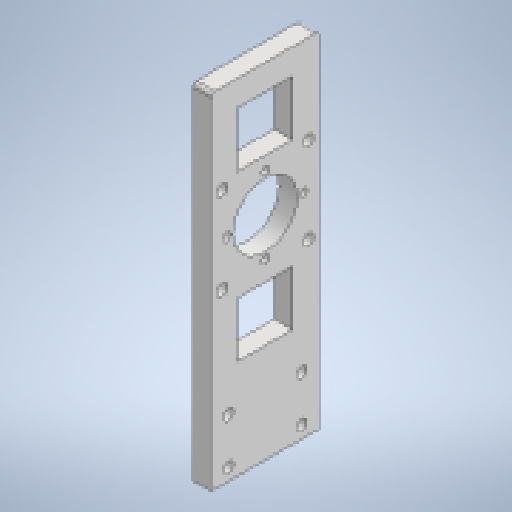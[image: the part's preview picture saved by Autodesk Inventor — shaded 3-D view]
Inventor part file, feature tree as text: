
AUTODESK INVENTOR PART (.ipt)
format: ipt  version: 2023 (Build 270158000, 158)  size: 200,192 bytes
history: native  units: mm
features: extrude x3, sketch x3
ambient origin geometry x8: Origin, YZ Plane, XZ Plane, XY Plane, X Axis, Y Axis, Z Axis, Center Point
bodies: Solid1 (feature_tree)
feature tree (6):
  extrude  "Extrusion1"  Depth=25.0mm
  extrude  "Extrusion2"  Depth=58.8mm
  extrude  "Extrusion3"  Depth=10.0mm TaperAngle=0.0deg
  sketch  "Sketch1"  dims[d0=6.0mm d1=25.0mm]
  sketch  "Sketch3"  dims[d2=40.0mm d3=58.8mm]
  sketch  "Sketch4"  dims[d4=38.2mm d5=10.0mm d6=0.0mm d7=150.0mm d8=2.0mm d9=30.0mm d12=60.0mm d13=16.0mm d14=10.0mm d15=0.0mm d16=47.14mm d17=6.0mm d18=56.4mm d19=35.0mm d20=20.0mm d21=0.0mm d22=42.0mm d23=4.5mm]
